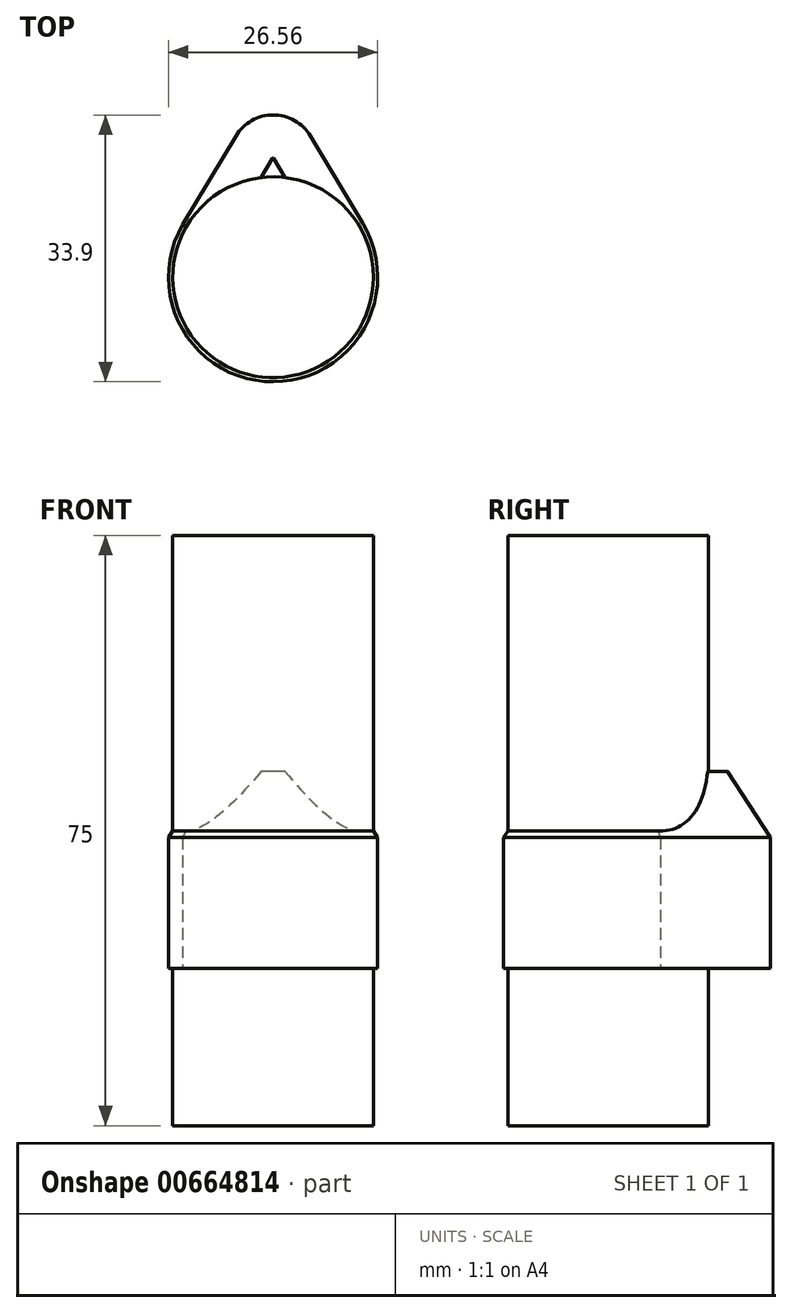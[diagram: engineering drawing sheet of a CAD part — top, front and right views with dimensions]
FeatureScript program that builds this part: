
annotation { "Feature Type Name" : "Feature", "Feature Type Description" : "" }
export const myFeature = defineFeature(function(context is Context, id is Id, definition is map)
    precondition{}
    {
        {
            var Q0;
            Q0=qCreatedBy(makeId("Top.planeOp"),FACE);
            var sketch = newSketch(context, id + "F0", { "sketchPlane" : qUnion([Q0])});
            skLineSegment(sketch, "E0", {"start": v(4.73, 17.94) * mm, "end": v(11.45, 6.73) * mm});
            skLineSegment(sketch, "E1", {"start": v(-4.73, 17.94) * mm, "end": v(-11.48, 6.67) * mm});
            skArc(sketch, "E2", {"start": v(4.73, 17.94) * mm, "mid": v(0, 20.62) * mm, "end": v(-4.73, 17.94) * mm});
            skCircle(sketch, "E3", {"center": v(0, 0) * mm, "radius": 13.28 * mm});
            skLineSegment(sketch, "E4", {"start": v(-11.48, 6.67) * mm, "end": v(11.45, 6.73) * mm});
            skPoint(sketch, "E5", {"position": v(-0.02, 6.7) * mm});
            skPoint(sketch, "E6", {"position": v(0, 17.94) * mm});
            skSolve(sketch);
        }
        {
            var Q0;
            {var subQ0=sQuery(id+"F0.wireOp",EDGE,"E2");Q0=makeQuery(id+"F0.imprint","IMPRINT",FACE,{"disambiguationData":[TD([[makeQuery(id+"F0.imprint","IMPRINT",EDGE,{"derivedFrom":subQ0}),1.0]])]});}
            var Q1;
            {var subQ0=sQuery(id+"F0.wireOp",EDGE,"E3");var subQ1=sQuery(id+"F0.wireOp",EDGE,"E1");var subQ2=makeQuery(id+"F0.imprint","INTERSECT",VERTEX,{"disambiguationData":[OD(0.0)],"derivedFrom":[subQ1,subQ0]});Q1=makeQuery(id+"F0.imprint","IMPRINT",FACE,{"disambiguationData":[TD([[makeQuery(id+"F0.imprint","IMPRINT",EDGE,{"disambiguationData":[TD([[subQ2,1.0]])],"derivedFrom":subQ1}),1.0]])]});}
            var Q2;
            {var subQ0=sQuery(id+"F0.wireOp",EDGE,"E4");var subQ1=sQuery(id+"F0.wireOp",EDGE,"E3");var subQ3=makeQuery(id+"F0.imprint","INTERSECT",VERTEX,{"derivedFrom":[subQ1,subQ0]});Q2=makeQuery(id+"F0.imprint","IMPRINT",FACE,{"disambiguationData":[TD([[makeQuery(id+"F0.imprint","IMPRINT",EDGE,{"disambiguationData":[TD([[subQ3,1.0]])],"derivedFrom":subQ1}),1.0]])]});}
            var Q3;
            {var subQ0=sQuery(id+"F0.wireOp",EDGE,"E3");var subQ1=sQuery(id+"F0.wireOp",EDGE,"E0");var subQ5=makeQuery(id+"F0.imprint","INTERSECT",VERTEX,{"disambiguationData":[OD(1.0)],"derivedFrom":[subQ1,subQ0]});Q3=makeQuery(id+"F0.imprint","IMPRINT",FACE,{"disambiguationData":[TD([[makeQuery(id+"F0.imprint","IMPRINT",EDGE,{"disambiguationData":[TD([[subQ5,1.0]])],"derivedFrom":subQ0}),1.0]])]});}
            extrude(context, id + "F1", {"entities" : qUnion([Q0, Q1, Q2, Q3]), "depth" : 25 * mm, "offsetDistance" : 25 * mm});
        }
        {
            var Q0;
            Q0=makeQuery(id+"F1.opExtrude","CAP_FACE",FACE,{"disambiguationData":[OSD([sQuery(id+"F0.wireOp",EDGE,"E0"),sQuery(id+"F0.wireOp",EDGE,"E1"),sQuery(id+"F0.wireOp",EDGE,"E2"),sQuery(id+"F0.wireOp",EDGE,"E3")])],"isStart":false});
            var sketch = newSketch(context, id + "F2", { "sketchPlane" : qUnion([Q0])});
            skCircle(sketch, "E7", {"center": v(0, 0) * mm, "radius": 12.75 * mm});
            skSolve(sketch);
        }
        {
            var Q0;
            Q0=makeQuery(id+"F2.imprint","IMPRINT",FACE,{"disambiguationData":[TD([[makeQuery(id+"F2.imprint","IMPRINT",EDGE,{"derivedFrom":sQuery(id+"F2.wireOp",EDGE,"E7")}),1.0]])]});
            extrude(context, id + "F3", {"entities" : qUnion([Q0]), "operationType" : NewBodyOperationType.ADD, "depth" : 30 * mm, "offsetDistance" : 25 * mm});
        }
        {
            var Q0;
            Q0=makeQuery(id+"F1.opExtrude","CAP_FACE",FACE,{"disambiguationData":[OSD([sQuery(id+"F0.wireOp",EDGE,"E0"),sQuery(id+"F0.wireOp",EDGE,"E1"),sQuery(id+"F0.wireOp",EDGE,"E2"),sQuery(id+"F0.wireOp",EDGE,"E3")])],"isStart":true});
            var sketch = newSketch(context, id + "F4", { "sketchPlane" : qUnion([Q0])});
            skCircle(sketch, "E8", {"center": v(0, 0) * mm, "radius": 12.75 * mm});
            skSolve(sketch);
        }
        {
            var Q0;
            Q0=makeQuery(id+"F4.imprint","IMPRINT",FACE,{"disambiguationData":[TD([[makeQuery(id+"F4.imprint","IMPRINT",EDGE,{"derivedFrom":sQuery(id+"F4.wireOp",EDGE,"E8")}),1.0]])]});
            extrude(context, id + "F5", {"entities" : qUnion([Q0]), "operationType" : NewBodyOperationType.ADD, "depth" : 20 * mm, "offsetDistance" : 25 * mm});
        }
        {
            var Q0;
            Q0=makeQuery(id+"F1.opExtrude","CAP_EDGE",EDGE,{"disambiguationData":[OSD([sQuery(id+"F0.wireOp",EDGE,"E0")])],"isStart":false});
            var Q1;
            Q1=makeQuery(id+"F1.opExtrude","CAP_EDGE",EDGE,{"disambiguationData":[OSD([sQuery(id+"F0.wireOp",EDGE,"E3")])],"isStart":false});
            chamfer(context, id + "F6", {"entities" : qUnion([Q0, Q1]), "chamferType" : ChamferType.OFFSET_ANGLE, "width" : 8.4 * mm, "oppositeDirection" : false, "angle" : 33 * degree, "tangentPropagation" : true});
        }
    });
